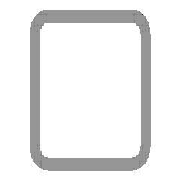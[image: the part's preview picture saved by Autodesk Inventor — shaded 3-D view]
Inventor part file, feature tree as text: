
AUTODESK INVENTOR PART (.ipt)
format: ipt  version: 2021 (Build 250183000, 183)  size: 150,528 bytes
history: native  units: mm (DEFAULTED — no unit token found)
features: other x6, sketch x3, split x2, extrude x1, plane x1
ambient origin geometry x8: Origin, YZ Plane, XZ Plane, XY Plane, X Axis, Y Axis, Z Axis, Center Point
bodies: Solid1 (feature_tree)
feature tree (13):
  parser-record x1  (decoder bookkeeping rows leaked as tree rows — omitted from the tree; the rows remain in map.json)
  other  "Driven Length"
  other  "Plano inicial"
  other  "Plano final"
  extrude  "Corpo"  TaperAngle=0.0deg  [1 undecoded]
  other  "Plano de trabalho4"
  split  "Dividir1"
  other  "Plano de trabalho5"
  split  "Dividir2"
  sketch  "Esboço"  dims[d11=50.8mm d12=4.7625mm d13=-25.4mm d14=2025.4mm d15=25.4mm d16=25.4mm d17=9.525mm d18=90.0deg d19=2050.8mm]
  sketch  "Sketch3"  dims[d3=2050.8mm d4=0.0mm]
  plane  "Work Plane3"
  sketch  "Sketch4"  dims[d10=50.8mm]
note: 1 required parameter value undecoded (feature->parameter linkage not recoverable at this tier; creation-order binding heuristic only, values carry confidence <= 0.55)
